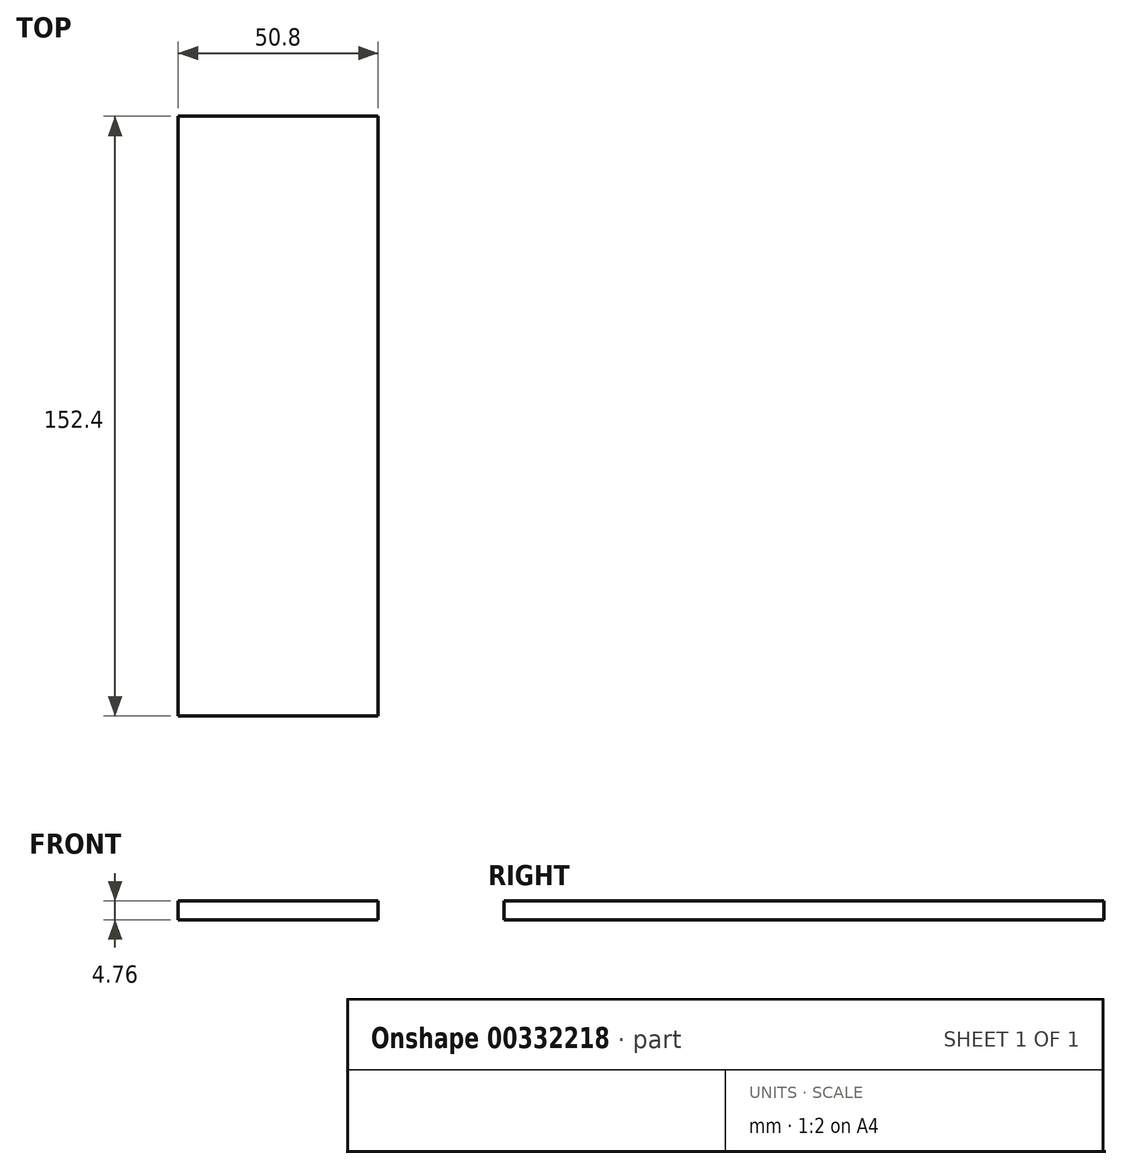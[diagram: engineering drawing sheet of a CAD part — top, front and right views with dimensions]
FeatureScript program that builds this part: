
annotation { "Feature Type Name" : "Feature", "Feature Type Description" : "" }
export const myFeature = defineFeature(function(context is Context, id is Id, definition is map)
    precondition{}
    {
        {
            var Q0;
            Q0=qCreatedBy(makeId("Top.planeOp"),FACE);
            var sketch = newSketch(context, id + "F0", { "sketchPlane" : qUnion([Q0])});
            skLineSegment(sketch, "E0.bottom", {"start": v(-17.37, -42.32) * mm, "end": v(33.43, -42.32) * mm});
            skLineSegment(sketch, "E0.top", {"start": v(-17.37, 110.08) * mm, "end": v(33.43, 110.08) * mm});
            skLineSegment(sketch, "E0.left", {"start": v(-17.37, -42.32) * mm, "end": v(-17.37, 110.08) * mm});
            skLineSegment(sketch, "E0.right", {"start": v(33.43, -42.32) * mm, "end": v(33.43, 110.08) * mm});
            skSolve(sketch);
        }
        {
            var Q0;
            Q0=makeQuery(id+"F0.imprint","IMPRINT",FACE,{"disambiguationData":[TD([[makeQuery(id+"F0.imprint","IMPRINT",EDGE,{"derivedFrom":sQuery(id+"F0.wireOp",EDGE,"E0.bottom")}),1.0]])]});
            extrude(context, id + "F1", {"entities" : qUnion([Q0]), "oppositeDirection" : true, "depth" : 4.76 * mm});
        }
    });
